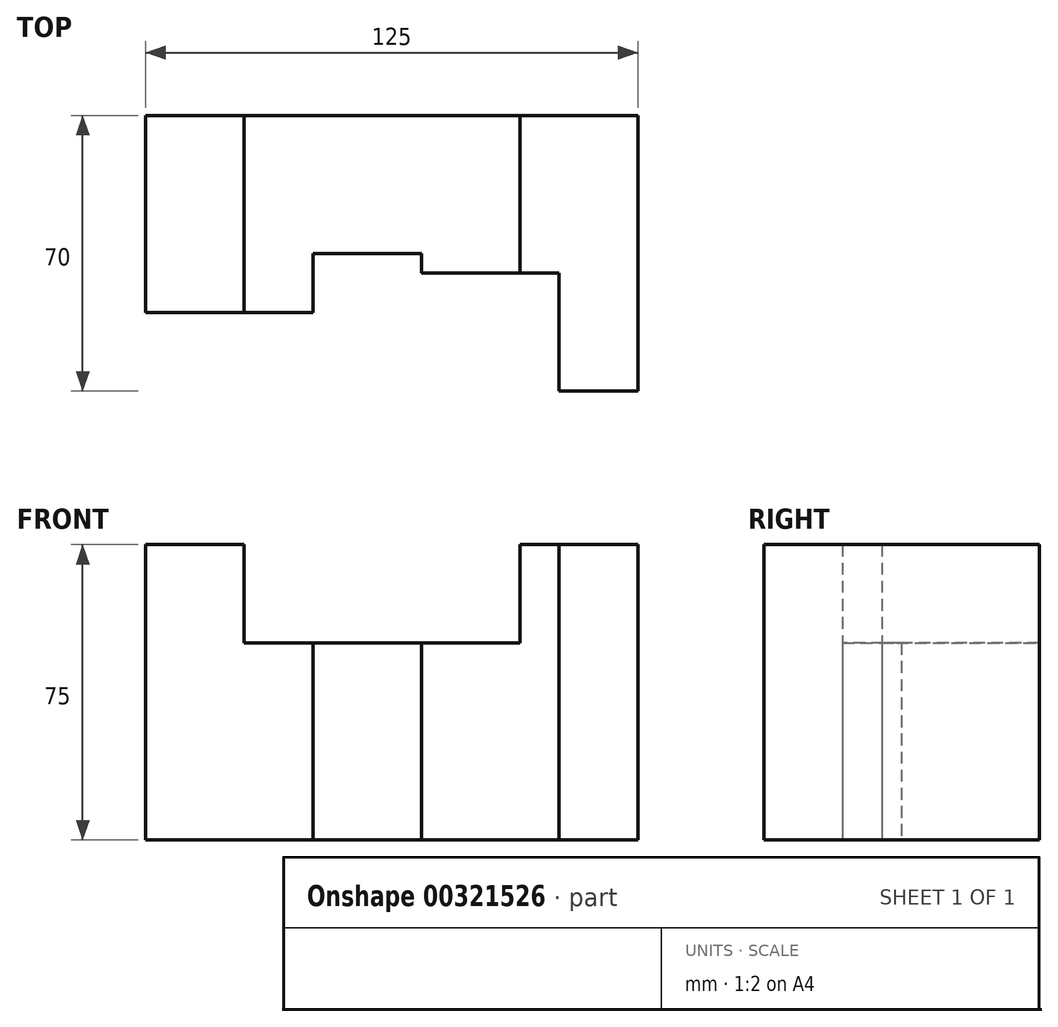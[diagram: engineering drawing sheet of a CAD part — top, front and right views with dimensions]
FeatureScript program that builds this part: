
annotation { "Feature Type Name" : "Feature", "Feature Type Description" : "" }
export const myFeature = defineFeature(function(context is Context, id is Id, definition is map)
    precondition{}
    {
        {
            var Q0;
            Q0=qCreatedBy(makeId("Top.planeOp"),FACE);
            var sketch = newSketch(context, id + "F0", { "sketchPlane" : qUnion([Q0])});
            skLineSegment(sketch, "E0", {"start": v(25, 0) * mm, "end": v(25, 50) * mm});
            skLineSegment(sketch, "E1", {"start": v(25, 50) * mm, "end": v(95, 50) * mm});
            skLineSegment(sketch, "E2", {"start": v(95, 50) * mm, "end": v(95, 10) * mm});
            skLineSegment(sketch, "E3", {"start": v(95, 10) * mm, "end": v(70, 10) * mm});
            skLineSegment(sketch, "E4", {"start": v(70, 10) * mm, "end": v(70, 15) * mm});
            skLineSegment(sketch, "E5", {"start": v(70, 15) * mm, "end": v(42.5, 15) * mm});
            skLineSegment(sketch, "E6", {"start": v(42.5, 15) * mm, "end": v(42.5, 0) * mm});
            skLineSegment(sketch, "E7", {"start": v(42.5, 0) * mm, "end": v(25, 0) * mm});
            skSolve(sketch);
        }
        {
            var Q0;
            Q0 = qSketchRegion(id + "F0", true);
            extrude(context, id + "F1", {"entities" : qUnion([Q0]), "depth" : 50 * mm});
        }
        {
            var Q0;
            Q0=qCreatedBy(makeId("Top.planeOp"),FACE);
            var sketch = newSketch(context, id + "F2", { "sketchPlane" : qUnion([Q0])});
            skLineSegment(sketch, "E8", {"start": v(0, 0) * mm, "end": v(25, 0) * mm});
            skLineSegment(sketch, "E9", {"start": v(25, 0) * mm, "end": v(25, 50) * mm});
            skLineSegment(sketch, "E10", {"start": v(25, 50) * mm, "end": v(0, 50) * mm});
            skLineSegment(sketch, "E11", {"start": v(0, 50) * mm, "end": v(0, 0) * mm});
            skSolve(sketch);
        }
        {
            var Q0;
            Q0 = qSketchRegion(id + "F2", true);
            extrude(context, id + "F3", {"entities" : qUnion([Q0]), "operationType" : NewBodyOperationType.ADD, "depth" : 75 * mm});
        }
        {
            var Q0;
            Q0=qCreatedBy(makeId("Top.planeOp"),FACE);
            var sketch = newSketch(context, id + "F4", { "sketchPlane" : qUnion([Q0])});
            skLineSegment(sketch, "E12", {"start": v(95, 50) * mm, "end": v(125, 50) * mm});
            skLineSegment(sketch, "E13", {"start": v(125, 50) * mm, "end": v(125, -20) * mm});
            skLineSegment(sketch, "E14", {"start": v(125, -20) * mm, "end": v(105, -20) * mm});
            skLineSegment(sketch, "E15", {"start": v(105, -20) * mm, "end": v(105, 10) * mm});
            skLineSegment(sketch, "E16", {"start": v(105, 10) * mm, "end": v(95, 10) * mm});
            skLineSegment(sketch, "E17", {"start": v(95, 10) * mm, "end": v(95, 50) * mm});
            skSolve(sketch);
        }
        {
            var Q0;
            Q0 = qSketchRegion(id + "F4", true);
            extrude(context, id + "F5", {"entities" : qUnion([Q0]), "operationType" : NewBodyOperationType.ADD, "depth" : 75 * mm});
        }
    });
